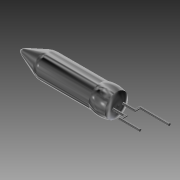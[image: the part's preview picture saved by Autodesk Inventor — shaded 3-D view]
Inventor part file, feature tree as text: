
AUTODESK INVENTOR PART (.ipt)
format: ipt  version: 2015 (Build 190159000, 159)  size: 944,128 bytes
history: native  units: mm
features: sketch x3, sweep x2, projected_geometry x2, revolve x1, plane x1
ambient origin geometry x8: Origin, YZ Plane, XZ Plane, XY Plane, X Axis, Y Axis, Z Axis, Center Point
bodies: Solid1 (feature_tree)
feature tree (9):
  revolve  "Revolution1"  [1 undecoded]
  sketch  "Sketch2"  dims[d9=0.5mm d10=5.0mm]
  plane  "Work Plane1"
  sketch  "Sketch3"  dims[d11=90.0deg d15=10.026647mm d16=2.0mm d19=5.0mm d20=0.0mm d21=2.0mm d22=90.0deg d23=12.0mm d24=90.0deg d25=5.0mm d26=0.0mm d27=2.0mm d28=90.0deg d29=8.0mm d30=24.25mm d31=0.9mm d32=0.9mm d33=0.0mm d34=0.0mm d35=0.0mm d36=0.0mm]
  sweep  "Sweep1"
  sweep  "Sweep2"
  sketch  "Sketch1"  dims[d6=7.0mm d7=4.75mm]
  projected_geometry  "Projected Loop1"
  projected_geometry  "Projected Loop2"
note: 1 required parameter value undecoded (feature->parameter linkage not recoverable at this tier; creation-order binding heuristic only, values carry confidence <= 0.55)
